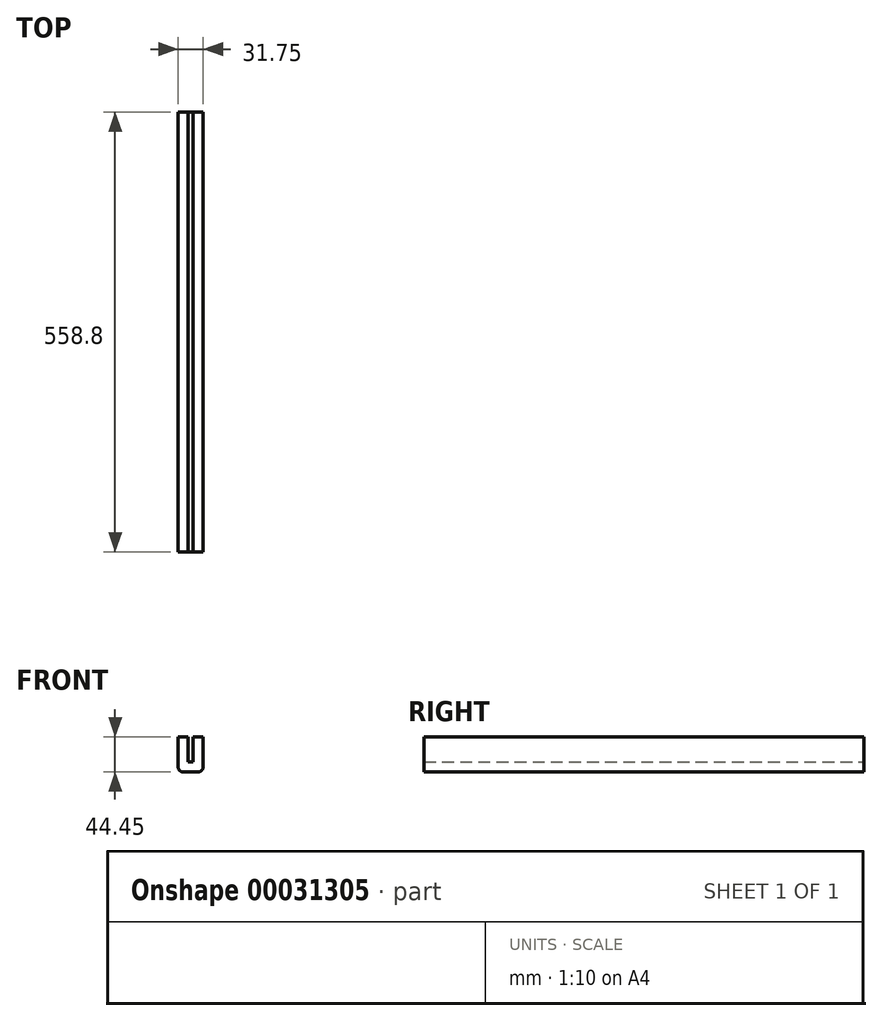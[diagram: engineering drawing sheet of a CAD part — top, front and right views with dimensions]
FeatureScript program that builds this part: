
annotation { "Feature Type Name" : "Feature", "Feature Type Description" : "" }
export const myFeature = defineFeature(function(context is Context, id is Id, definition is map)
    precondition{}
    {
        {
            var Q0;
            Q0=qCreatedBy(makeId("Front.planeOp"),FACE);
            var sketch = newSketch(context, id + "F0", { "sketchPlane" : qUnion([Q0])});
            skLineSegment(sketch, "E0.bottom", {"start": v(0, 0) * mm, "end": v(-31.75, 0) * mm});
            skLineSegment(sketch, "E0.left", {"start": v(0, 0) * mm, "end": v(0, 44.45) * mm});
            skLineSegment(sketch, "E1", {"start": v(-31.75, 0) * mm, "end": v(-31.75, 44.45) * mm});
            skLineSegment(sketch, "E2", {"start": v(-31.75, 44.45) * mm, "end": v(-19.05, 44.45) * mm});
            skLineSegment(sketch, "E3", {"start": v(-19.05, 44.45) * mm, "end": v(-19.05, 12.7) * mm});
            skLineSegment(sketch, "E4", {"start": v(-19.05, 12.7) * mm, "end": v(-12.7, 12.7) * mm});
            skLineSegment(sketch, "E5", {"start": v(-12.7, 12.7) * mm, "end": v(-12.7, 44.45) * mm});
            skLineSegment(sketch, "E6", {"start": v(-12.7, 44.45) * mm, "end": v(0, 44.45) * mm});
            skSolve(sketch);
        }
        {
            var Q0;
            Q0=makeQuery(id+"F0.imprint","IMPRINT",FACE,{"disambiguationData":[TD([[makeQuery(id+"F0.imprint","IMPRINT",EDGE,{"derivedFrom":sQuery(id+"F0.wireOp",EDGE,"E0.bottom")}),-1.0]])]});
            extrude(context, id + "F1", {"entities" : qUnion([Q0]), "depth" : 558.8 * mm});
        }
        {
            var Q0;
            Q0=makeQuery(id+"F1.opExtrude","SWEPT_EDGE",EDGE,{"disambiguationData":[OSD([sQuery(id+"F0.wireOp",EDGE,"E0.bottom"),sQuery(id+"F0.wireOp",EDGE,"E0.left")])]});
            var Q1;
            Q1=makeQuery(id+"F1.opExtrude","SWEPT_EDGE",EDGE,{"disambiguationData":[OSD([sQuery(id+"F0.wireOp",EDGE,"E0.bottom"),sQuery(id+"F0.wireOp",EDGE,"E1")])]});
            fillet(context, id + "F2", {"entities" : qUnion([Q0, Q1]), "radius" : 6.35 * mm, "tangentPropagation" : true, "allowEdgeOverflow" : false});
        }
    });
